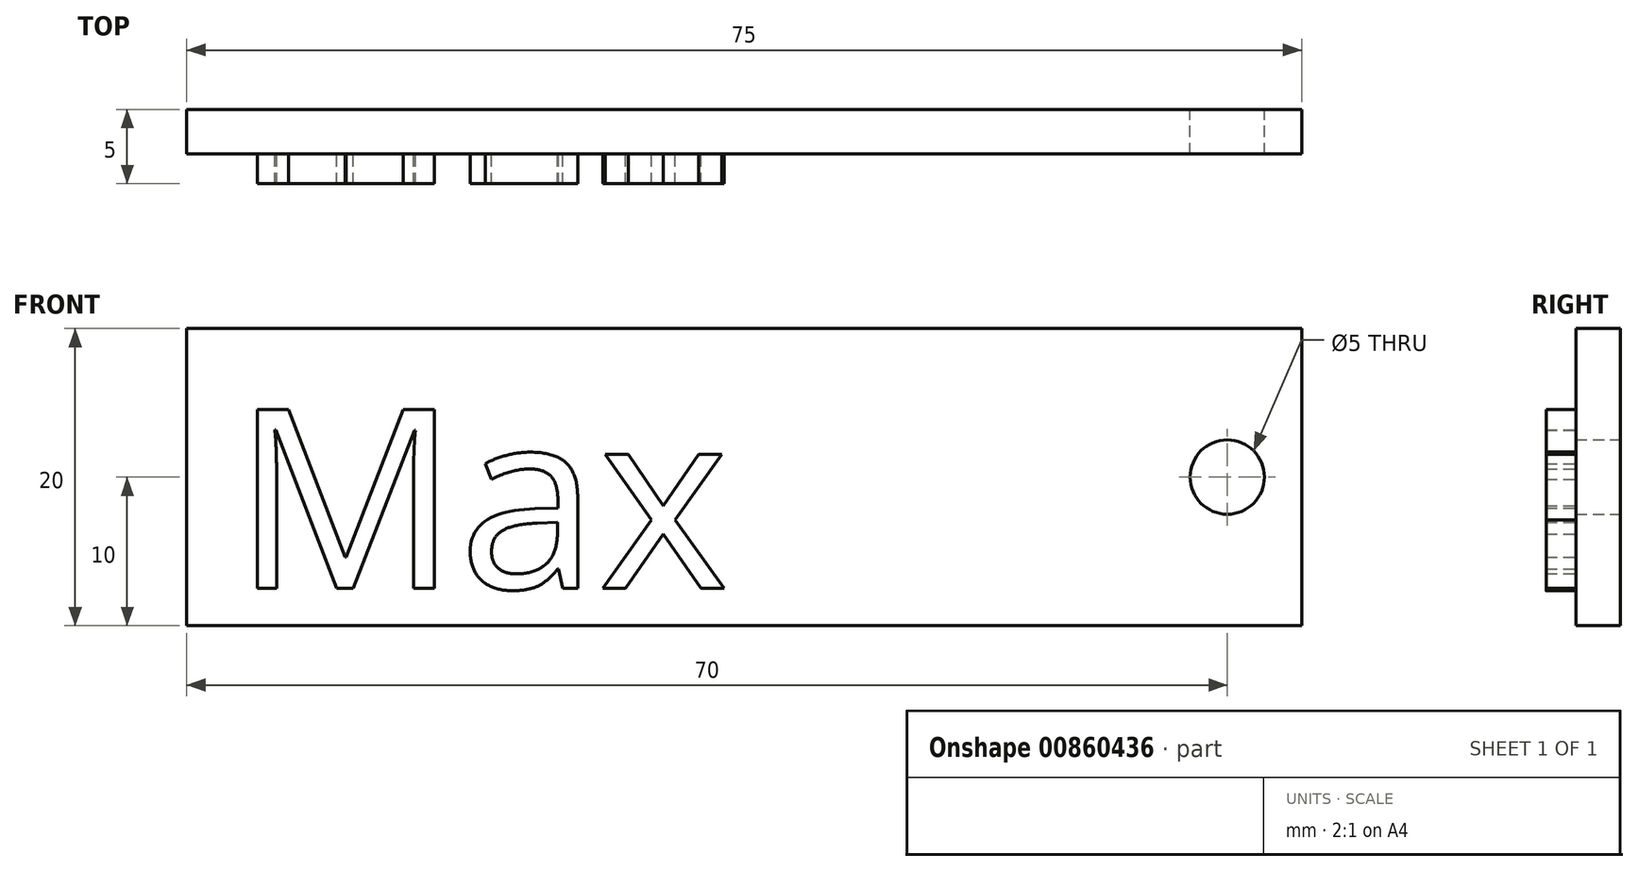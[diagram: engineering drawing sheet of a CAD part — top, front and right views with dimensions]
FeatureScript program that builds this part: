
annotation { "Feature Type Name" : "Feature", "Feature Type Description" : "" }
export const myFeature = defineFeature(function(context is Context, id is Id, definition is map)
    precondition{}
    {
        {
            var Q0;
            Q0=qCreatedBy(makeId("Front.planeOp"),FACE);
            var sketch = newSketch(context, id + "F0", { "sketchPlane" : qUnion([Q0])});
            skLineSegment(sketch, "E0.bottom", {"start": v(0, 0) * mm, "end": v(75, 0) * mm});
            skLineSegment(sketch, "E0.top", {"start": v(0, -20) * mm, "end": v(75, -20) * mm});
            skLineSegment(sketch, "E0.left", {"start": v(0, 0) * mm, "end": v(0, -20) * mm});
            skLineSegment(sketch, "E0.right", {"start": v(75, 0) * mm, "end": v(75, -20) * mm});
            skCircle(sketch, "E1", {"center": v(70, -10) * mm, "radius": 2.5 * mm});
            skSolve(sketch);
        }
        {
            var Q0;
            Q0 = qSketchRegion(id + "F0", true);
            extrude(context, id + "F1", {"entities" : qUnion([Q0]), "depth" : 3 * mm, "offsetDistance" : 25 * mm});
        }
        {
            var Q0;
            Q0=makeQuery(id+"F1.opExtrude","CAP_FACE",FACE,{"disambiguationData":[OSD([sQuery(id+"F0.wireOp",EDGE,"E0.bottom"),sQuery(id+"F0.wireOp",EDGE,"E0.top"),sQuery(id+"F0.wireOp",EDGE,"E0.left"),sQuery(id+"F0.wireOp",EDGE,"E0.right"),sQuery(id+"F0.wireOp",EDGE,"E1")])],"isStart":false});
            var sketch = newSketch(context, id + "F2", { "sketchPlane" : qUnion([Q0])});
            skText(sketch, "E2", { "text": "Max", "fontName": "OpenSans-Regular.ttf"});
            const initialGuessF2  = {"E2": [0.0031, -0.01748, 1, 0, 0.01212]};
            skSetInitialGuess(sketch, initialGuessF2);
            skSolve(sketch);
        }
        {
            var Q0;
            Q0 = qSketchRegion(id + "F2", true);
            extrude(context, id + "F3", {"entities" : qUnion([Q0]), "operationType" : NewBodyOperationType.ADD, "depth" : 2 * mm, "offsetDistance" : 25 * mm});
        }
    });
